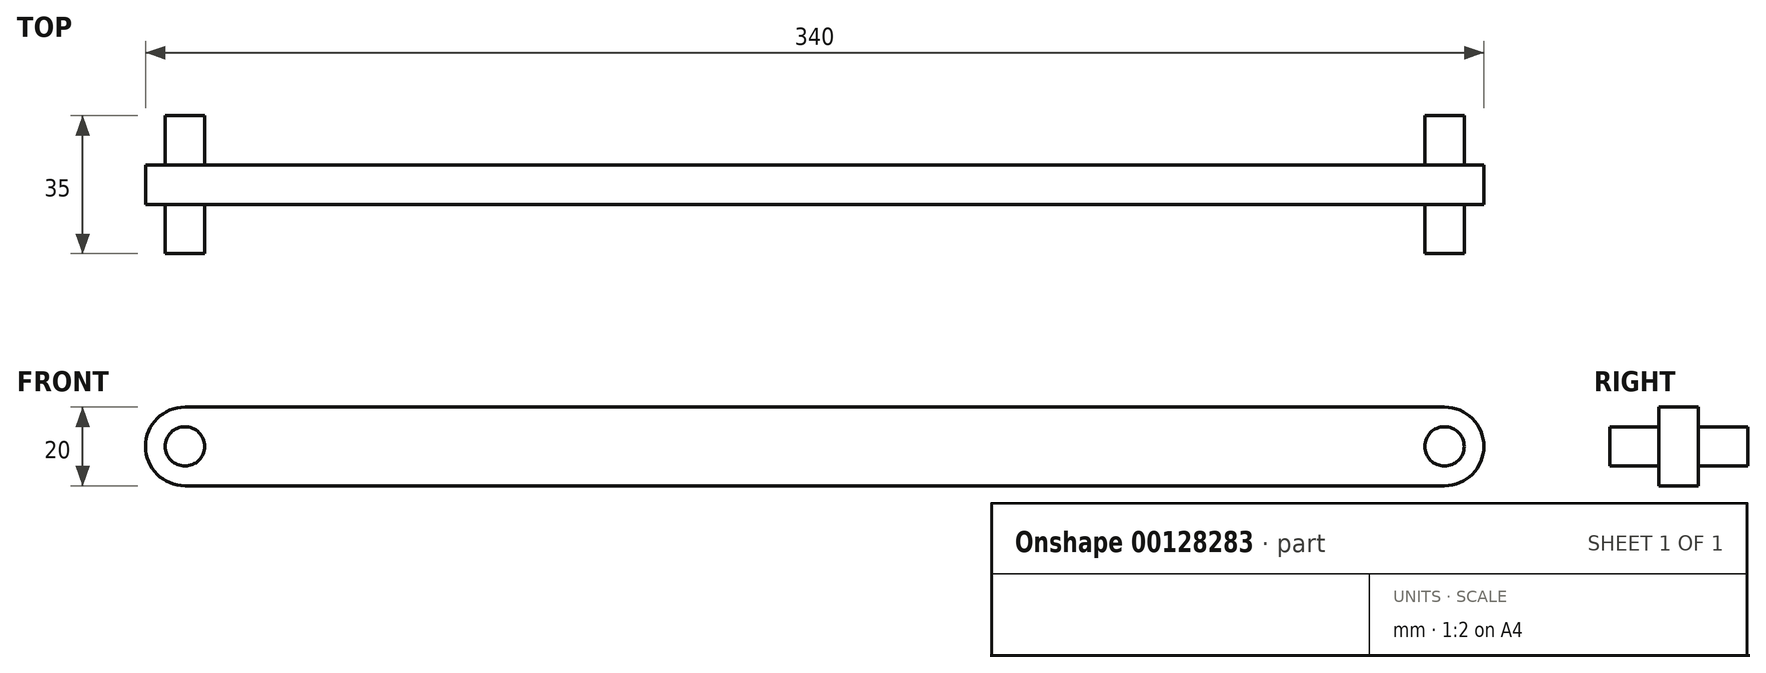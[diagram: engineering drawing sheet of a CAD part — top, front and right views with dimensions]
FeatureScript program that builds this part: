
annotation { "Feature Type Name" : "Feature", "Feature Type Description" : "" }
export const myFeature = defineFeature(function(context is Context, id is Id, definition is map)
    precondition{}
    {
        {
            var Q0;
            Q0=qCreatedBy(makeId("Front.planeOp"),FACE);
            var sketch = newSketch(context, id + "F0", { "sketchPlane" : qUnion([Q0])});
            skArc(sketch, "E0", {"start": v(0, 10) * mm, "mid": v(-10, 0) * mm, "end": v(0, -10) * mm});
            skArc(sketch, "E1", {"start": v(320, -10) * mm, "mid": v(330, 0) * mm, "end": v(320, 10) * mm});
            skLineSegment(sketch, "E2", {"start": v(0, -10) * mm, "end": v(320, -10) * mm});
            skLineSegment(sketch, "E3", {"start": v(320, 10) * mm, "end": v(0, 10) * mm});
            skCircle(sketch, "E4", {"center": v(0, 0) * mm, "radius": 5 * mm});
            skCircle(sketch, "E5", {"center": v(320, 0) * mm, "radius": 5 * mm});
            skSolve(sketch);
        }
        {
            var Q0;
            Q0 = qSketchRegion(id + "F0", true);
            extrude(context, id + "F1", {"entities" : qUnion([Q0]), "depth" : 10 * mm});
        }
        {
            var Q0;
            Q0=qCreatedBy(makeId("Front.planeOp"),FACE);
            cPlane(context, id + "F2", {"entities" : qUnion([Q0]), "cplaneType" : CPlaneType.OFFSET, "offset" : 12.5 * mm, "oppositeDirection" : true, "width" : 150 * mm, "height" : 150 * mm});
        }
        {
            var Q0;
            Q0=qCreatedBy(id+"F2.planeOp",FACE);
            var sketch = newSketch(context, id + "F3", { "sketchPlane" : qUnion([Q0])});
            skCircle(sketch, "E6", {"center": v(0, 0) * mm, "radius": 5 * mm});
            skCircle(sketch, "E7", {"center": v(320, 0) * mm, "radius": 5 * mm});
            skSolve(sketch);
        }
        {
            var Q0;
            Q0 = qSketchRegion(id + "F3", true);
            extrude(context, id + "F4", {"entities" : qUnion([Q0]), "operationType" : NewBodyOperationType.ADD, "depth" : 35 * mm});
        }
    });
